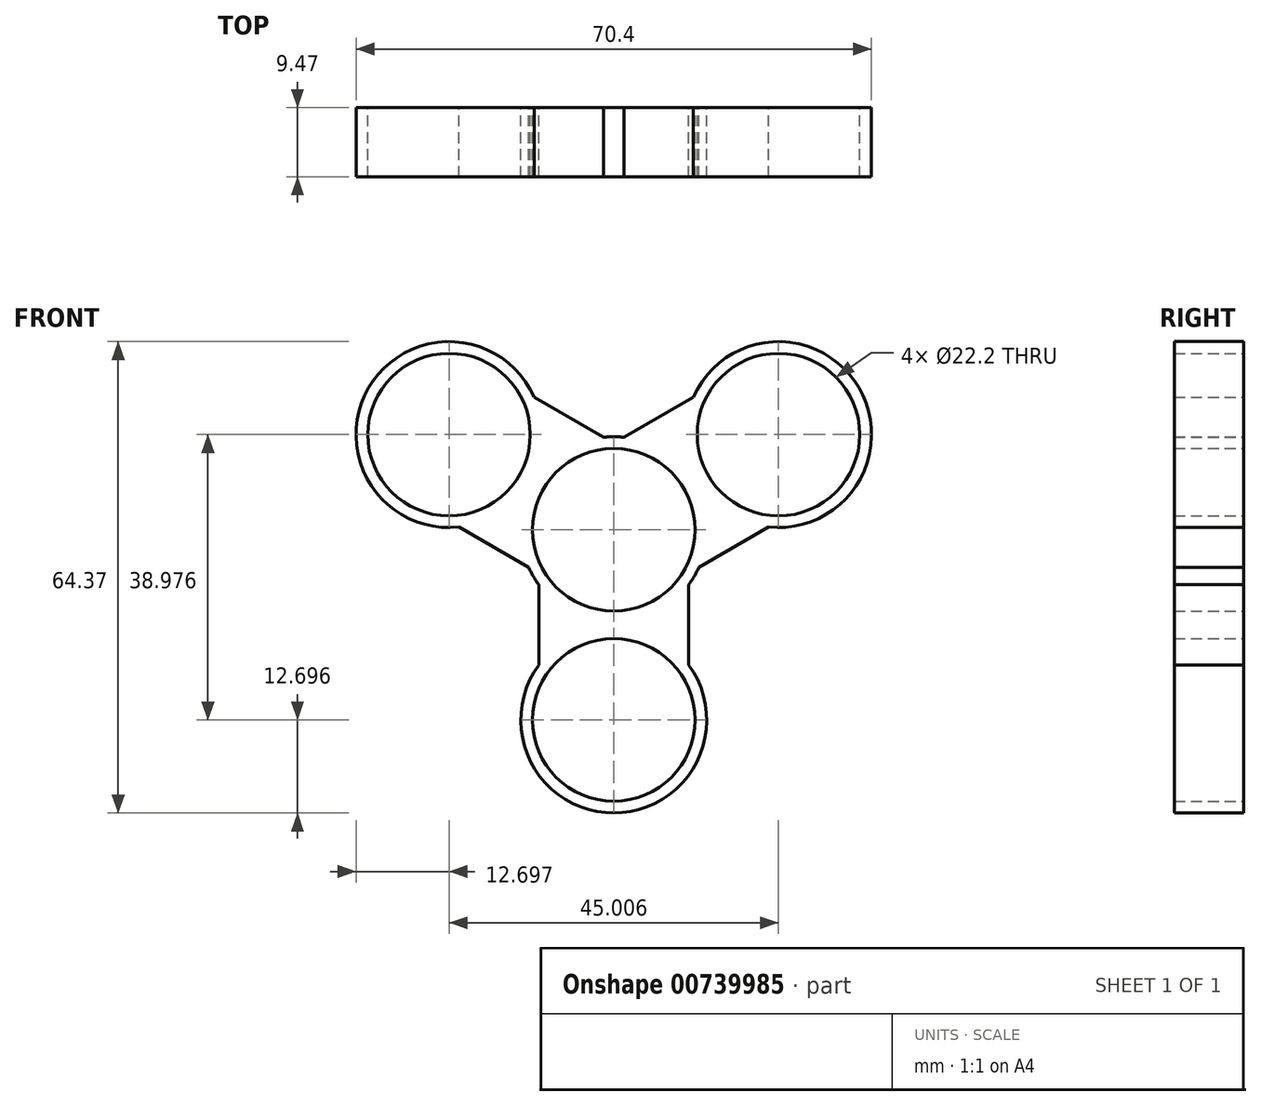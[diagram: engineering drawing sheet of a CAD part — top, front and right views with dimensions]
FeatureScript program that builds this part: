
annotation { "Feature Type Name" : "Feature", "Feature Type Description" : "" }
export const myFeature = defineFeature(function(context is Context, id is Id, definition is map)
    precondition{}
    {
        {
            var Q0;
            Q0=qCreatedBy(makeId("Front.planeOp"),FACE);
            var sketch = newSketch(context, id + "F0", { "sketchPlane" : qUnion([Q0])});
            skCircle(sketch, "E0", {"center": v(0, 0) * mm, "radius": 11.1 * mm});
            skCircle(sketch, "E1", {"center": v(0, -25.98) * mm, "radius": 11.1 * mm});
            skArc(sketch, "E2", {"start": v(10.25, -7.5) * mm, "mid": v(11, -6.35) * mm, "end": v(11.62, -5.12) * mm});
            skArc(sketch, "E3", {"start": v(-10.25, -18.48) * mm, "mid": v(0, -38.68) * mm, "end": v(10.25, -18.48) * mm});
            skLineSegment(sketch, "E4", {"start": v(-10.25, -18.48) * mm, "end": v(-10.25, -7.5) * mm});
            skLineSegment(sketch, "E5", {"start": v(10.25, -7.5) * mm, "end": v(10.25, -18.48) * mm});
            skArc(sketch, "E6.1.0", {"start": v(21.13, 0.37) * mm, "mid": v(33.5, 19.34) * mm, "end": v(10.88, 18.12) * mm});
            skCircle(sketch, "E6.1.1", {"center": v(22.5, 13) * mm, "radius": 11.1 * mm});
            skLineSegment(sketch, "E6.1.2", {"start": v(1.37, 12.63) * mm, "end": v(10.88, 18.12) * mm});
            skLineSegment(sketch, "E6.1.3", {"start": v(21.13, 0.37) * mm, "end": v(11.62, -5.12) * mm});
            skArc(sketch, "E6.2.0", {"start": v(-10.88, 18.12) * mm, "mid": v(-33.5, 19.34) * mm, "end": v(-21.13, 0.37) * mm});
            skCircle(sketch, "E6.2.1", {"center": v(-22.5, 13) * mm, "radius": 11.1 * mm});
            skLineSegment(sketch, "E6.2.2", {"start": v(-11.62, -5.12) * mm, "end": v(-21.13, 0.37) * mm});
            skLineSegment(sketch, "E6.2.3", {"start": v(-10.88, 18.12) * mm, "end": v(-1.37, 12.63) * mm});
            skArc(sketch, "E7.trimOffspring", {"start": v(-11.62, -5.12) * mm, "mid": v(-11, -6.35) * mm, "end": v(-10.25, -7.5) * mm});
            skArc(sketch, "E8.trimOffspring", {"start": v(1.37, 12.63) * mm, "mid": v(0, 12.7) * mm, "end": v(-1.37, 12.63) * mm});
            skSolve(sketch);
        }
        {
            var Q0;
            Q0=makeQuery(id+"F0.imprint","IMPRINT",FACE,{"disambiguationData":[TD([[makeQuery(id+"F0.imprint","IMPRINT",EDGE,{"derivedFrom":sQuery(id+"F0.wireOp",EDGE,"E0")}),-1.0]])]});
            extrude(context, id + "F1", {"entities" : qUnion([Q0]), "depth" : 9.47 * mm, "offsetDistance" : 25.4 * mm});
        }
    });
